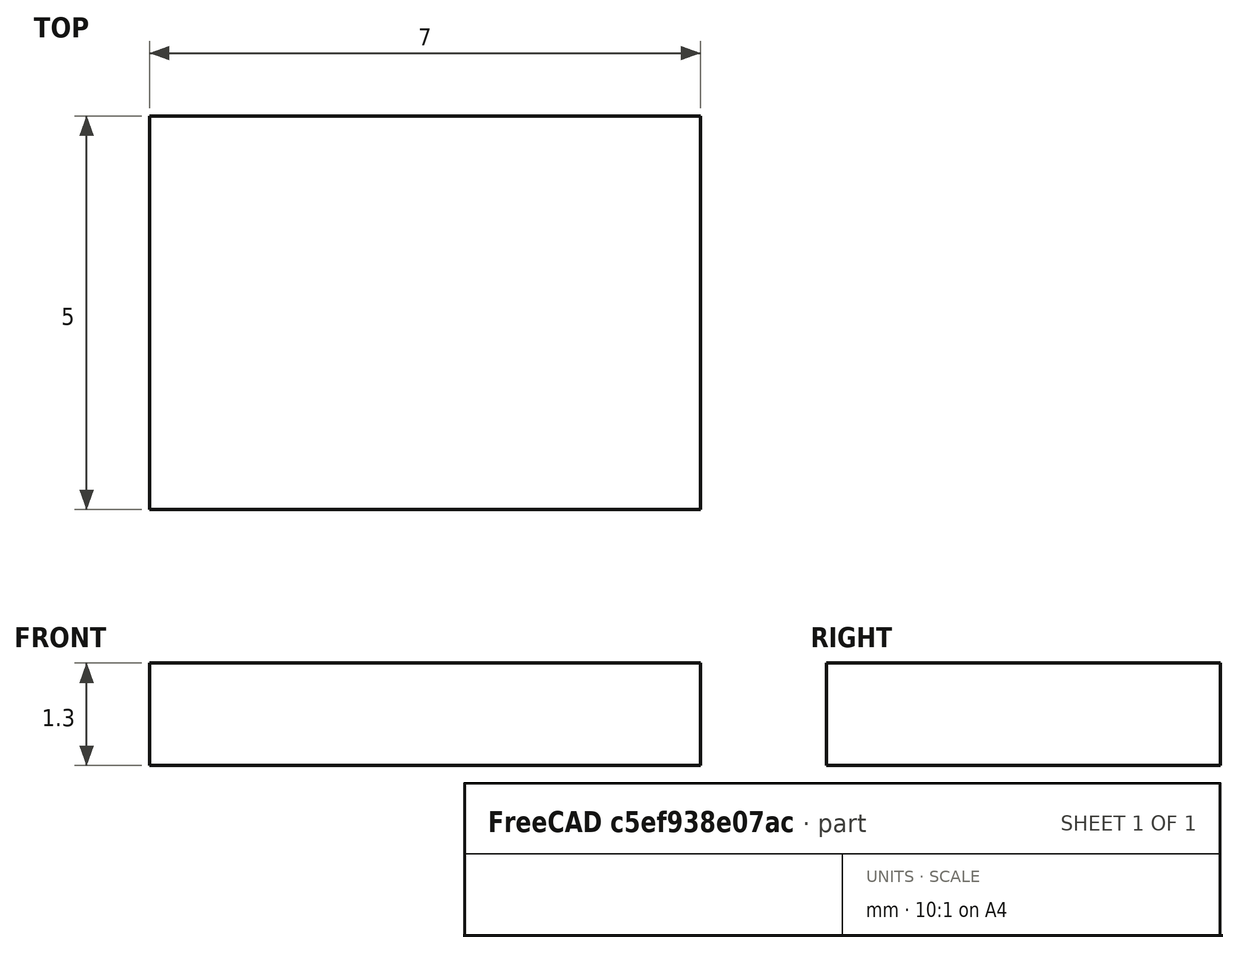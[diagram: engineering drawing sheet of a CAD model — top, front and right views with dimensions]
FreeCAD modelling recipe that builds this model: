
FCSTD DOCUMENT  (FreeCAD 0.17R13541 (Git))
Label: SMD-XTAL
License: All rights reserved
LicenseURL: http://en.wikipedia.org/wiki/All_rights_reserved
objects: Sketcher::SketchObject×1, PartDesign::Pad×1, PartDesign::Body×1
note: 4 computed .brp shape members not serialized (recipe doc carries the construction recipe); baked Part::Feature solids carry a one-line shape summary decoded from their .brp

FEATURE [Sketcher::SketchObject] Sketch
  MapMode = 5
  Support = -> [XY_Plane]
  sketch-geometry (4):
    g0: LineSegment StartX=0 StartY=0 StartZ=0 EndX=7 EndY=0 EndZ=0
    g1: LineSegment StartX=7 StartY=0 StartZ=0 EndX=7 EndY=5 EndZ=0
    g2: LineSegment StartX=7 StartY=5 StartZ=0 EndX=0 EndY=5 EndZ=0
    g3: LineSegment StartX=0 StartY=5 StartZ=0 EndX=0 EndY=0 EndZ=0
  constraints (8):
    c: Coincident(g0,g1)
    c: Coincident(g1,g2)
    c: Coincident(g2,g3)
    c: Coincident(g3,g0)
    c: Horizontal(g0)
    c: Horizontal(g2)
    c: Vertical(g1)
    c: Vertical(g3)
FEATURE [PartDesign::Pad] Pad
  Length = 1.3
  Length2 = 100
  Profile = -> Sketch
  Type = 0
FEATURE [PartDesign::Body] Body
  Group = -> [Sketch,Pad]
  Origin = -> Origin
  Tip = -> Pad
